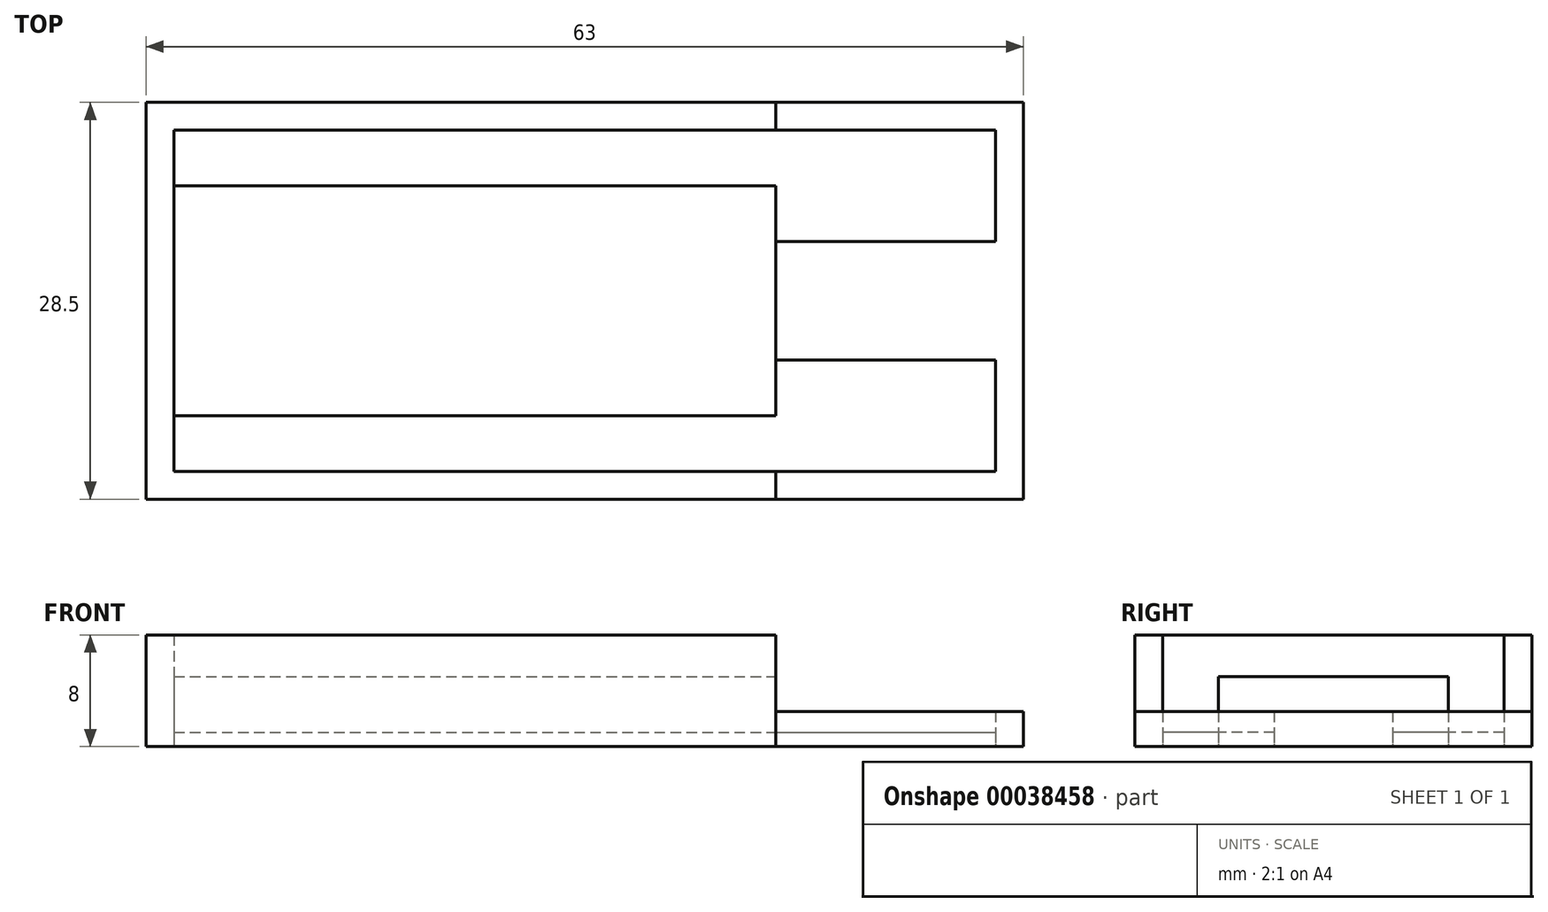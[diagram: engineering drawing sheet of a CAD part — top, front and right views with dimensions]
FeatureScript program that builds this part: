
annotation { "Feature Type Name" : "Feature", "Feature Type Description" : "" }
export const myFeature = defineFeature(function(context is Context, id is Id, definition is map)
    precondition{}
    {
        {
            var Q0;
            Q0=qCreatedBy(makeId("Top.planeOp"),FACE);
            var sketch = newSketch(context, id + "F0", { "sketchPlane" : qUnion([Q0])});
            skLineSegment(sketch, "E0", {"start": v(-83.28, 24.5) * mm, "end": v(93.04, 24.5) * mm, "construction": true});
            skLineSegment(sketch, "E1", {"start": v(59, -21.37) * mm, "end": v(59, 62.02) * mm, "construction": true});
            skLineSegment(sketch, "E2", {"start": v(-82.03, 20.5) * mm, "end": v(90.12, 20.5) * mm, "construction": true});
            skLineSegment(sketch, "E3", {"start": v(-82.58, 4) * mm, "end": v(90.12, 4) * mm, "construction": true});
            skLineSegment(sketch, "E4", {"start": v(43.2, 55.46) * mm, "end": v(43.2, -21.13) * mm, "construction": true});
            skLineSegment(sketch, "E5", {"start": v(-2, 34.22) * mm, "end": v(-2, -12.72) * mm, "construction": true});
            skLineSegment(sketch, "E6", {"start": v(-8.23, 26.5) * mm, "end": v(67.64, 26.5) * mm, "construction": true});
            skLineSegment(sketch, "E7", {"start": v(61, 36.16) * mm, "end": v(61, -15.62) * mm, "construction": true});
            skLineSegment(sketch, "E8", {"start": v(68.06, -2) * mm, "end": v(-8.92, -2) * mm, "construction": true});
            skLineSegment(sketch, "E9", {"start": v(34.9, 16.5) * mm, "end": v(73.13, 16.5) * mm, "construction": true});
            skLineSegment(sketch, "E10", {"start": v(34.68, 8) * mm, "end": v(73.78, 8) * mm, "construction": true});
            skLineSegment(sketch, "E11.bottom", {"start": v(59, 26.5) * mm, "end": v(61, 26.5) * mm});
            skLineSegment(sketch, "E11.top", {"start": v(59, -2) * mm, "end": v(61, -2) * mm});
            skLineSegment(sketch, "E11.left", {"start": v(59, 26.5) * mm, "end": v(59, -2) * mm});
            skLineSegment(sketch, "E11.right", {"start": v(61, 26.5) * mm, "end": v(61, -2) * mm});
            skLineSegment(sketch, "E12.bottom", {"start": v(43.2, 26.5) * mm, "end": v(59, 26.5) * mm});
            skLineSegment(sketch, "E12.top", {"start": v(43.2, 24.5) * mm, "end": v(59, 24.5) * mm});
            skLineSegment(sketch, "E12.left", {"start": v(43.2, 26.5) * mm, "end": v(43.2, 24.5) * mm});
            skLineSegment(sketch, "E12.right", {"start": v(59, 26.5) * mm, "end": v(59, 24.5) * mm});
            skLineSegment(sketch, "E13.top", {"start": v(43.2, 16.5) * mm, "end": v(59, 16.5) * mm});
            skLineSegment(sketch, "E13.left", {"start": v(43.2, 24.5) * mm, "end": v(43.2, 16.5) * mm});
            skLineSegment(sketch, "E13.right", {"start": v(59, 24.5) * mm, "end": v(59, 16.5) * mm});
            skLineSegment(sketch, "E14.top", {"start": v(43.2, 8) * mm, "end": v(59, 8) * mm});
            skLineSegment(sketch, "E14.left", {"start": v(43.2, 16.5) * mm, "end": v(43.2, 8) * mm});
            skLineSegment(sketch, "E14.right", {"start": v(59, 16.5) * mm, "end": v(59, 8) * mm});
            skLineSegment(sketch, "E15.top", {"start": v(43.2, 0) * mm, "end": v(59, 0) * mm});
            skLineSegment(sketch, "E15.left", {"start": v(43.2, 8) * mm, "end": v(43.2, 0) * mm});
            skLineSegment(sketch, "E15.right", {"start": v(59, 8) * mm, "end": v(59, 0) * mm});
            skLineSegment(sketch, "E16.top", {"start": v(43.2, -2) * mm, "end": v(59, -2) * mm});
            skLineSegment(sketch, "E16.left", {"start": v(43.2, 0) * mm, "end": v(43.2, -2) * mm});
            skLineSegment(sketch, "E16.right", {"start": v(59, 0) * mm, "end": v(59, -2) * mm});
            skLineSegment(sketch, "E17.bottom", {"start": v(0, 24.5) * mm, "end": v(43.2, 24.5) * mm});
            skLineSegment(sketch, "E17.top", {"start": v(0, 20.5) * mm, "end": v(43.2, 20.5) * mm});
            skLineSegment(sketch, "E17.left", {"start": v(0, 24.5) * mm, "end": v(0, 20.5) * mm});
            skLineSegment(sketch, "E17.right", {"start": v(43.2, 24.5) * mm, "end": v(43.2, 20.5) * mm});
            skLineSegment(sketch, "E18.top", {"start": v(0, 4) * mm, "end": v(43.2, 4) * mm});
            skLineSegment(sketch, "E18.left", {"start": v(0, 20.5) * mm, "end": v(0, 4) * mm});
            skLineSegment(sketch, "E18.right", {"start": v(43.2, 20.5) * mm, "end": v(43.2, 4) * mm});
            skLineSegment(sketch, "E19.top", {"start": v(0, 0) * mm, "end": v(43.2, 0) * mm});
            skLineSegment(sketch, "E19.left", {"start": v(0, 4) * mm, "end": v(0, 0) * mm});
            skLineSegment(sketch, "E19.right", {"start": v(43.2, 4) * mm, "end": v(43.2, 0) * mm});
            skLineSegment(sketch, "E20", {"start": v(43.2, 26.5) * mm, "end": v(-2, 26.5) * mm});
            skLineSegment(sketch, "E21", {"start": v(-2, 26.5) * mm, "end": v(-2, -2) * mm});
            skLineSegment(sketch, "E22", {"start": v(-2, -2) * mm, "end": v(43.2, -2) * mm});
            skSolve(sketch);
        }
        {
            var Q0;
            Q0=makeQuery(id+"F0.imprint","IMPRINT",FACE,{"disambiguationData":[TD([[makeQuery(id+"F0.imprint","IMPRINT",EDGE,{"derivedFrom":sQuery(id+"F0.wireOp",EDGE,"E12.top")}),-1.0]])]});
            var Q1;
            {var subQ1=sQuery(id+"F0.wireOp",EDGE,"E14.top");Q1=makeQuery(id+"F0.imprint","IMPRINT",FACE,{"disambiguationData":[TD([[makeQuery(id+"F0.imprint","IMPRINT",EDGE,{"derivedFrom":subQ1}),-1.0]])]});}
            var Q2;
            Q2=makeQuery(id+"F0.imprint","IMPRINT",FACE,{"disambiguationData":[TD([[makeQuery(id+"F0.imprint","IMPRINT",EDGE,{"derivedFrom":sQuery(id+"F0.wireOp",EDGE,"E17.bottom")}),-1.0]])]});
            var Q3;
            Q3=makeQuery(id+"F0.imprint","IMPRINT",FACE,{"disambiguationData":[TD([[makeQuery(id+"F0.imprint","IMPRINT",EDGE,{"derivedFrom":sQuery(id+"F0.wireOp",EDGE,"E18.top")}),-1.0]])]});
            extrude(context, id + "F1", {"entities" : qUnion([Q0, Q1, Q2, Q3]), "depth" : 1 * mm});
        }
        {
            var Q0;
            Q0=makeQuery(id+"F0.imprint","IMPRINT",FACE,{"disambiguationData":[TD([[makeQuery(id+"F0.imprint","IMPRINT",EDGE,{"derivedFrom":sQuery(id+"F0.wireOp",EDGE,"E12.bottom")}),-1.0]])]});
            var Q1;
            {var subQ0=sQuery(id+"F0.wireOp",EDGE,"E13.top");Q1=makeQuery(id+"F0.imprint","IMPRINT",FACE,{"disambiguationData":[TD([[makeQuery(id+"F0.imprint","IMPRINT",EDGE,{"derivedFrom":subQ0}),-1.0]])]});}
            var Q2;
            Q2=makeQuery(id+"F0.imprint","IMPRINT",FACE,{"disambiguationData":[TD([[makeQuery(id+"F0.imprint","IMPRINT",EDGE,{"derivedFrom":sQuery(id+"F0.wireOp",EDGE,"E15.top")}),-1.0]])]});
            var Q3;
            Q3=makeQuery(id+"F0.imprint","IMPRINT",FACE,{"disambiguationData":[TD([[makeQuery(id+"F0.imprint","IMPRINT",EDGE,{"derivedFrom":sQuery(id+"F0.wireOp",EDGE,"E11.bottom")}),-1.0]])]});
            extrude(context, id + "F2", {"entities" : qUnion([Q0, Q1, Q2, Q3]), "depth" : 2.5 * mm});
        }
        {
            var Q0;
            {var subQ4=sQuery(id+"F0.wireOp",EDGE,"E17.top");Q0=makeQuery(id+"F0.imprint","IMPRINT",FACE,{"disambiguationData":[TD([[makeQuery(id+"F0.imprint","IMPRINT",EDGE,{"derivedFrom":subQ4}),-1.0]])]});}
            extrude(context, id + "F3", {"entities" : qUnion([Q0]), "depth" : 5 * mm});
        }
        {
            var Q0;
            Q0=makeQuery(id+"F0.imprint","IMPRINT",FACE,{"disambiguationData":[TD([[makeQuery(id+"F0.imprint","IMPRINT",EDGE,{"derivedFrom":sQuery(id+"F0.wireOp",EDGE,"E12.left")}),-1.0]])]});
            extrude(context, id + "F4", {"entities" : qUnion([Q0]), "depth" : 8 * mm});
        }
    });
